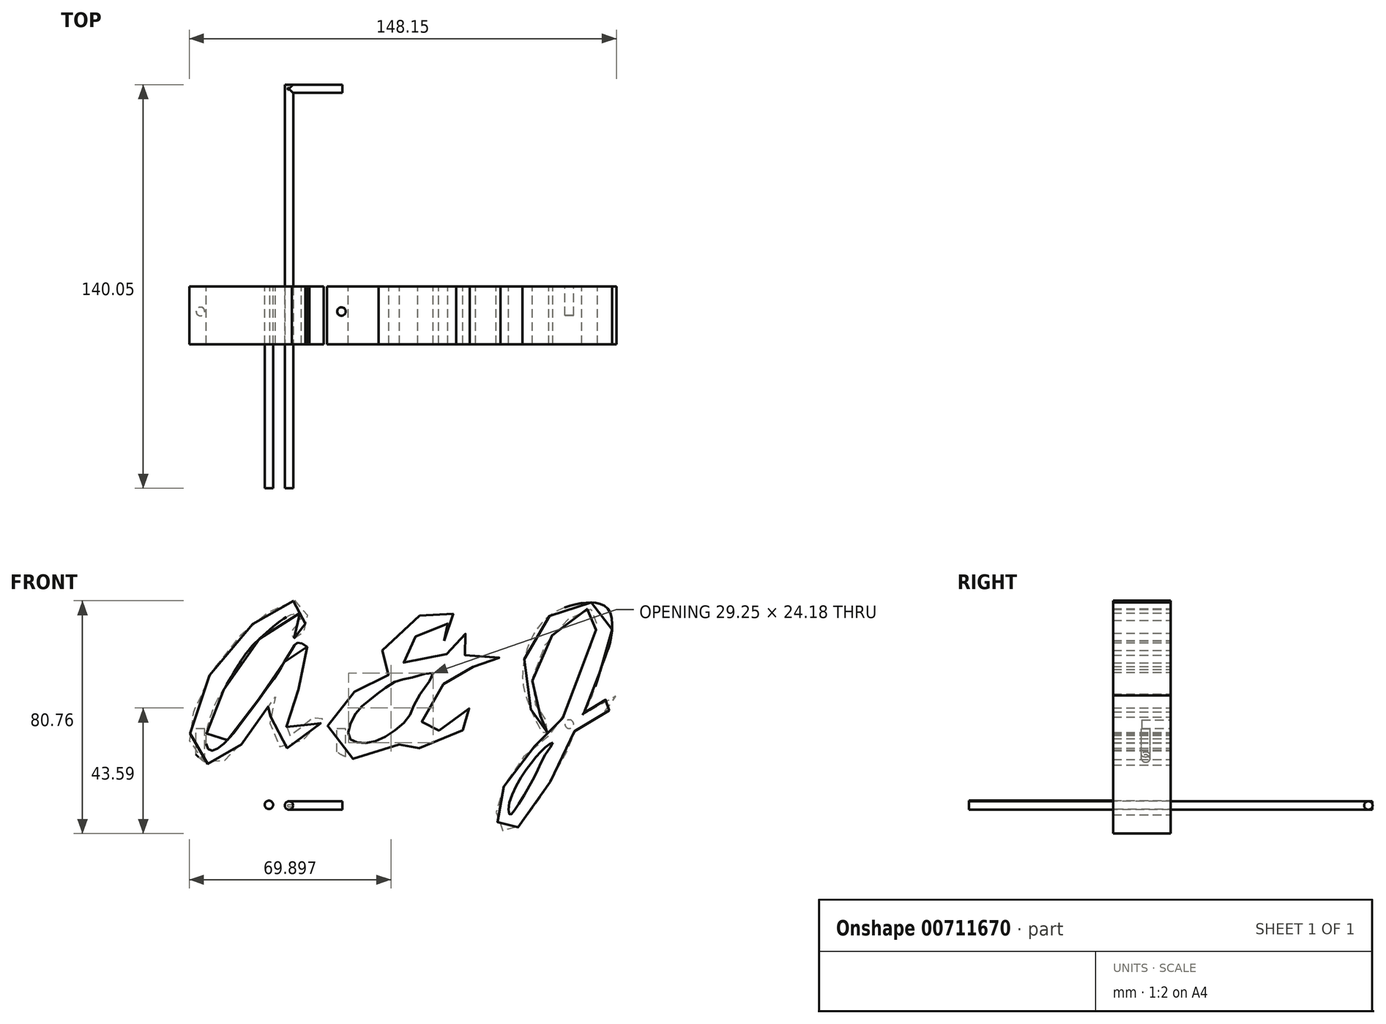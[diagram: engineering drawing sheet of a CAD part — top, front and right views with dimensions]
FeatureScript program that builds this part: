
annotation { "Feature Type Name" : "Feature", "Feature Type Description" : "" }
export const myFeature = defineFeature(function(context is Context, id is Id, definition is map)
    precondition{}
    {
        {
            var Q0;
            Q0=qCreatedBy(makeId("Front.planeOp"),FACE);
            var sketch = newSketch(context, id + "F0", { "sketchPlane" : qUnion([Q0])});
            skPoint(sketch, "E0.36.internal.snap0", {"position": v(-74.58, 4.4) * mm});
            skFitSpline(sketch, "E0", {"points": [v(-37.76, 31.34) * mm, v(-36, 30.71) * mm, v(-34.92, 31.72) * mm, v(-34.42, 33.48) * mm, v(-33.73, 35.31) * mm, v(-33.85, 36.5) * mm, v(-33.16, 38.46) * mm, v(-33.41, 41.23) * mm, v(-34.6, 43.7) * mm, v(-38.9, 44.26) * mm, v(-44.19, 41.86) * mm, v(-49.16, 38.78) * mm, v(-57.1, 31.66) * mm, v(-65.27, 21.41) * mm, v(-72.24, 7.7) * mm, v(-73.66, -0.77) * mm, v(-74.04, -4.06) * mm, v(-72.46, -8.03) * mm, v(-69.02, -11.33) * mm, v(-66.32, -12.53) * mm, v(-63.02, -11.63) * mm, v(-58.38, -8.03) * mm, v(-53.95, -2.56) * mm, v(-51.63, 1.18) * mm, v(-47.51, 6.5) * mm, v(-44.29, 12.12) * mm, v(-44.44, 10.17) * mm, v(-45.34, 6.73) * mm, v(-46.16, 0) * mm, v(-44.59, -4.51) * mm, v(-41.74, -6.54) * mm, v(-37.54, -5.94) * mm, v(-33.65, -3.09) * mm, v(-29.83, 0) * mm, v(-27.65, 5.53) * mm, v(-29.23, 5.75) * mm, v(-30.65, 4.4) * mm, v(-34.25, 1.26) * mm, v(-38.9, -2.41) * mm, v(-40.84, -3.31) * mm, v(-40.62, -1.22) * mm, v(-40.32, 1.93) * mm, v(-39.5, 6.05) * mm, v(-37.1, 11) * mm, v(-35.75, 15.42) * mm, v(-33.57, 23.06) * mm, v(-32.52, 27.4) * mm, v(-35, 29.58) * mm, v(-37.02, 29.66) * mm, v(-38.37, 27.78) * mm, v(-40.92, 23.51) * mm, v(-43.31, 19.47) * mm, v(-46.99, 14.3) * mm, v(-51.26, 8.45) * mm, v(-56.88, 0.96) * mm, v(-60.25, -3.24) * mm, v(-65.2, -7.28) * mm, v(-67.37, -7.13) * mm, v(-68.27, -3.76) * mm, v(-67.3, 2.3) * mm, v(-65.04, 8.68) * mm, v(-61.67, 14.37) * mm, v(-54.63, 25.84) * mm, v(-48.7, 32.2) * mm, v(-39.86, 39.13) * mm, v(-36.83, 40.08) * mm, v(-35.51, 39.98) * mm, v(-35.51, 37.96) * mm, v(-37.26, 35.42) * mm, v(-38.48, 33.73) * mm, v(-37.76, 31.34) * mm]});
            skFitSpline(sketch, "E1", {"points": [v(14.32, 30.5) * mm, v(16.5, 31.34) * mm, v(18.37, 34.63) * mm, v(17.77, 39.05) * mm, v(16.2, 41.23) * mm, v(11.7, 40.78) * mm, v(6.9, 39.65) * mm, v(1.88, 36.95) * mm, v(-5.39, 29.84) * mm, v(-8.46, 23.54) * mm, v(-7.4, 20.84) * mm, v(-5.39, 19.47) * mm, v(-4.86, 18.82) * mm, v(-5.84, 18.45) * mm, v(-11, 16.12) * mm, v(-15.43, 13.8) * mm, v(-20.75, 9.6) * mm, v(-24.5, 5.48) * mm, v(-26.3, -1.49) * mm, v(-24.12, -6.88) * mm, v(-16.85, -10.48) * mm, v(-7.78, -9.28) * mm, v(-1.94, -6.13) * mm, v(1.96, -1.71) * mm, v(2.1, -2.31) * mm, v(3.53, -4.7) * mm, v(6.83, -7.18) * mm, v(13.95, -5.38) * mm, v(21.21, 0) * mm, v(24.81, 3.98) * mm, v(25.19, 5.86) * mm, v(23.84, 7.2) * mm, v(22.49, 6.68) * mm, v(19.42, 3.6) * mm, v(14.55, 0.69) * mm, v(10.35, -1.56) * mm, v(5.4, -1.86) * mm, v(5.4, 0) * mm, v(7.2, 3.68) * mm, v(9.83, 8.68) * mm, v(13.05, 13.87) * mm, v(17.62, 20.47) * mm, v(18.37, 20.62) * mm, v(20.77, 21.07) * mm, v(28.03, 21.67) * mm, v(31.93, 21.74) * mm, v(33.73, 22.5) * mm, v(33.28, 25.19) * mm, v(31.7, 26.99) * mm, v(24.44, 26.24) * mm, v(21.14, 25.64) * mm, v(20.77, 26.09) * mm, v(23.01, 28.86) * mm, v(22.71, 31.34) * mm, v(21.89, 32.83) * mm, v(20.54, 33.13) * mm, v(19.12, 31.34) * mm, v(16.57, 27.66) * mm, v(15, 25.86) * mm, v(9.23, 24.07) * mm, v(1.96, 22.87) * mm, v(-1.04, 23.62) * mm, v(-0.74, 25.86) * mm, v(2.33, 29.76) * mm, v(6, 33.73) * mm, v(11.92, 37.48) * mm, v(15.52, 37.03) * mm, v(15.07, 35.75) * mm, v(13.57, 34.33) * mm, v(12.6, 33.13) * mm, v(12.6, 31.34) * mm, v(14.32, 30.5) * mm]});
            skFitSpline(sketch, "E2", {"points": [v(50.15, -1.2) * mm, v(50.56, -0.75) * mm, v(50.51, 0.69) * mm, v(49.53, 3.26) * mm, v(47.8, 4.42) * mm, v(45.97, 8.68) * mm, v(44.87, 15.36) * mm, v(47.65, 25.77) * mm, v(54.02, 35.07) * mm, v(61.88, 40.94) * mm, v(65.55, 41.47) * mm, v(67.12, 39.82) * mm, v(67.35, 36) * mm, v(65.62, 29.76) * mm, v(61.88, 20.62) * mm, v(58.43, 12.1) * mm, v(53.56, 0) * mm, v(49.56, -3.15) * mm, v(41.62, -10.02) * mm, v(35.13, -19.73) * mm, v(32.6, -27.04) * mm, v(32.67, -31.78) * mm, v(34.26, -34.86) * mm, v(36.59, -36.34) * mm, v(40.3, -33.8) * mm, v(46.65, -25.42) * mm, v(58, -5.38) * mm, v(59.63, -0.6) * mm, v(62.76, 1.38) * mm, v(72.26, 7.07) * mm, v(74.04, 11) * mm, v(73.3, 11.58) * mm, v(70.18, 9.99) * mm, v(62.6, 4.16) * mm, v(62.02, 4.16) * mm, v(62.97, 5.86) * mm, v(66.1, 12.64) * mm, v(69.65, 23.66) * mm, v(71.83, 29.76) * mm, v(72.01, 40.18) * mm, v(67.82, 43.48) * mm, v(61.4, 43.48) * mm, v(52.32, 40.18) * mm, v(45.01, 32.2) * mm, v(41.63, 20.62) * mm, v(43.23, 9.62) * mm, v(47.95, -0.72) * mm, v(48.17, -1.02) * mm, v(48.58, -1.21) * mm, v(50.15, -1.2) * mm]});
            skFitSpline(sketch, "E3", {"points": [v(10.46, 19.34) * mm, v(3.84, 17.9) * mm, v(-1.39, 16.88) * mm, v(-6.93, 13.55) * mm, v(-11.97, 9.64) * mm, v(-16.07, 5.86) * mm, v(-18.9, -0.57) * mm, v(-18.27, -3.53) * mm, v(-15.19, -4.85) * mm, v(-9.77, -4.41) * mm, v(-3.02, -0.7) * mm, v(2.2, 4.47) * mm, v(5.23, 10.9) * mm, v(10.46, 19.34) * mm]});
            skFitSpline(sketch, "E4", {"points": [v(52.05, -4.85) * mm, v(50.96, -5.3) * mm, v(48.64, -7.05) * mm, v(45.68, -10.43) * mm, v(41.9, -15.45) * mm, v(37.77, -23.24) * mm, v(36.64, -28.16) * mm, v(37.11, -29.73) * mm, v(37.55, -29.73) * mm, v(38.5, -28.57) * mm, v(42.87, -21.74) * mm, v(46.7, -14.39) * mm, v(49.56, -8.73) * mm, v(52.05, -4.85) * mm]});
            skCircle(sketch, "E5", {"center": v(-46.48, -26.36) * mm, "radius": 1.45 * mm});
            skCircle(sketch, "E6", {"center": v(-39.52, -26.59) * mm, "radius": 1.45 * mm});
            skSolve(sketch);
        }
        {
            var Q0;
            Q0=makeQuery(id+"F0.imprint","IMPRINT",FACE,{"disambiguationData":[TD([[makeQuery(id+"F0.imprint","IMPRINT",EDGE,{"derivedFrom":sQuery(id+"F0.wireOp",EDGE,"E0")}),1.0]])]});
            var Q1;
            Q1=makeQuery(id+"F0.imprint","IMPRINT",FACE,{"disambiguationData":[TD([[makeQuery(id+"F0.imprint","IMPRINT",EDGE,{"derivedFrom":sQuery(id+"F0.wireOp",EDGE,"E1")}),1.0]])]});
            var Q2;
            Q2=makeQuery(id+"F0.imprint","IMPRINT",FACE,{"disambiguationData":[TD([[makeQuery(id+"F0.imprint","IMPRINT",EDGE,{"derivedFrom":sQuery(id+"F0.wireOp",EDGE,"E2")}),1.0]])]});
            extrude(context, id + "F1", {"entities" : qUnion([Q0, Q1, Q2]), "depth" : 20 * mm, "offsetDistance" : 25 * mm});
        }
        {
            var Q0;
            Q0=makeQuery(id+"F1.opExtrude","CAP_FACE",FACE,{"disambiguationData":[OSD([sQuery(id+"F0.wireOp",EDGE,"E2"),sQuery(id+"F0.wireOp",EDGE,"E4")])],"isStart":true});
            var sketch = newSketch(context, id + "F2", { "sketchPlane" : qUnion([Q0])});
            skCircle(sketch, "E7", {"center": v(-57.74, 1.63) * mm, "radius": 1.5 * mm});
            skSolve(sketch);
        }
        {
            var Q0;
            Q0=makeQuery(id+"F2.imprint","IMPRINT",FACE,{"disambiguationData":[TD([[makeQuery(id+"F2.imprint","IMPRINT",EDGE,{"derivedFrom":sQuery(id+"F2.wireOp",EDGE,"E7")}),1.0]])]});
            extrude(context, id + "F3", {"entities" : qUnion([Q0]), "operationType" : NewBodyOperationType.REMOVE, "oppositeDirection" : true, "depth" : 10 * mm, "offsetDistance" : 25 * mm});
        }
        {
            var Q0;
            Q0=qCreatedBy(makeId("Top.planeOp"),FACE);
            var sketch = newSketch(context, id + "F4", { "sketchPlane" : qUnion([Q0])});
            skCircle(sketch, "E8", {"center": v(-21.34, -8.65) * mm, "radius": 1.5 * mm});
            skCircle(sketch, "E9", {"center": v(-70.24, -8.65) * mm, "radius": 1.5 * mm});
            skSolve(sketch);
        }
        {
            var Q0;
            Q0=makeQuery(id+"F4.imprint","IMPRINT",FACE,{"disambiguationData":[TD([[makeQuery(id+"F4.imprint","IMPRINT",EDGE,{"derivedFrom":sQuery(id+"F4.wireOp",EDGE,"E8")}),1.0]])]});
            extrude(context, id + "F5", {"entities" : qUnion([Q0]), "operationType" : NewBodyOperationType.REMOVE, "oppositeDirection" : true, "depth" : 13.2 * mm, "offsetDistance" : 25 * mm});
        }
        {
            var Q0;
            Q0=makeQuery(id+"F4.imprint","IMPRINT",FACE,{"disambiguationData":[TD([[makeQuery(id+"F4.imprint","IMPRINT",EDGE,{"derivedFrom":sQuery(id+"F4.wireOp",EDGE,"E9")}),1.0]])]});
            extrude(context, id + "F6", {"entities" : qUnion([Q0]), "operationType" : NewBodyOperationType.REMOVE, "oppositeDirection" : true, "depth" : 25 * mm, "offsetDistance" : 25 * mm});
        }
        {
            var Q0;
            Q0=makeQuery(id+"F0.imprint","IMPRINT",FACE,{"disambiguationData":[TD([[makeQuery(id+"F0.imprint","IMPRINT",EDGE,{"derivedFrom":sQuery(id+"F0.wireOp",EDGE,"E5")}),1.0]])]});
            extrude(context, id + "F7", {"entities" : qUnion([Q0]), "depth" : 70 * mm, "offsetDistance" : 25 * mm});
        }
        {
            var Q0;
            Q0=makeQuery(id+"F0.imprint","IMPRINT",FACE,{"disambiguationData":[TD([[makeQuery(id+"F0.imprint","IMPRINT",EDGE,{"derivedFrom":sQuery(id+"F0.wireOp",EDGE,"E6")}),1.0]])]});
            extrude(context, id + "F8", {"entities" : qUnion([Q0]), "endBound" : BoundingType.SYMMETRIC, "oppositeDirection" : true, "depth" : 140 * mm, "offsetDistance" : 25 * mm});
        }
        {
            var Q0;
            Q0=qCreatedBy(makeId("Right.planeOp"),FACE);
            var sketch = newSketch(context, id + "F9", { "sketchPlane" : qUnion([Q0])});
            skCircle(sketch, "E10", {"center": v(68.6, -26.58) * mm, "radius": 1.45 * mm});
            skSolve(sketch);
        }
        {
            var Q0;
            Q0=makeQuery(id+"F9.imprint","IMPRINT",FACE,{"disambiguationData":[TD([[makeQuery(id+"F9.imprint","IMPRINT",EDGE,{"derivedFrom":sQuery(id+"F9.wireOp",EDGE,"E10")}),1.0]])]});
            extrude(context, id + "F10", {"entities" : qUnion([Q0]), "operationType" : NewBodyOperationType.ADD, "oppositeDirection" : true, "depth" : 39.92 * mm, "offsetDistance" : 25 * mm, "hasSecondDirection" : true, "secondDirectionOppositeDirection" : true, "secondDirectionDepth" : 21 * mm});
        }
    });
